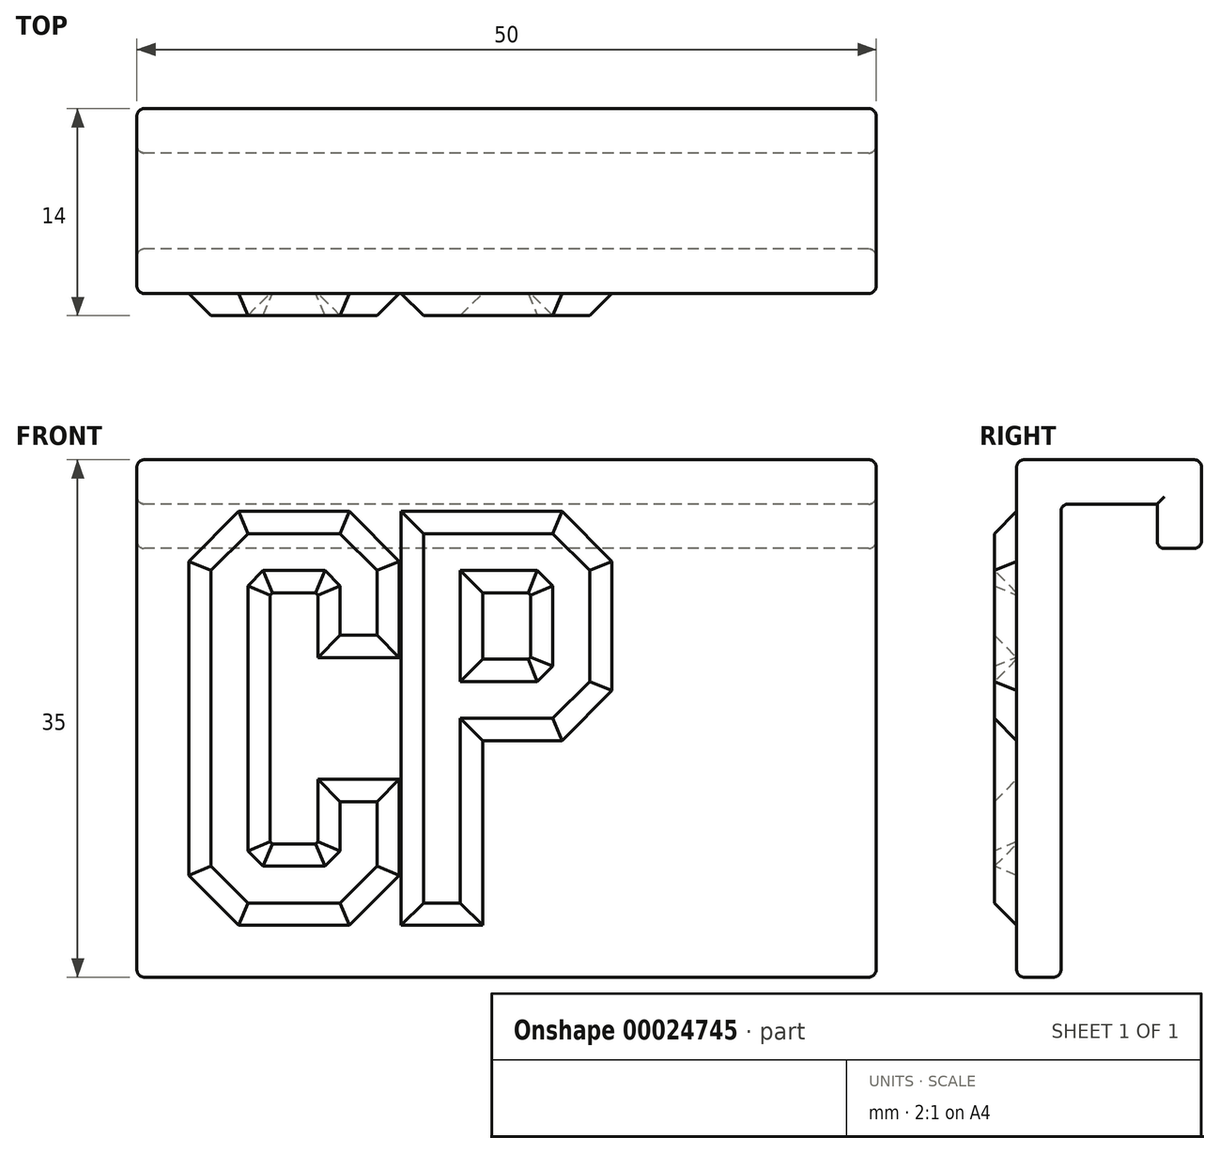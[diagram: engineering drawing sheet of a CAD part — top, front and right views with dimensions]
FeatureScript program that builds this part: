
annotation { "Feature Type Name" : "Feature", "Feature Type Description" : "" }
export const myFeature = defineFeature(function(context is Context, id is Id, definition is map)
    precondition{}
    {
        {
            var Q0;
            Q0=qCreatedBy(makeId("Right.planeOp"),FACE);
            var sketch = newSketch(context, id + "F0", { "sketchPlane" : qUnion([Q0])});
            skLineSegment(sketch, "E0", {"start": v(0, 0) * mm, "end": v(0, 35) * mm});
            skLineSegment(sketch, "E1", {"start": v(0, 35) * mm, "end": v(12.5, 35) * mm});
            skLineSegment(sketch, "E2", {"start": v(12.5, 35) * mm, "end": v(12.5, 29) * mm});
            skLineSegment(sketch, "E3", {"start": v(12.5, 29) * mm, "end": v(9.5, 29) * mm});
            skLineSegment(sketch, "E4", {"start": v(9.5, 29) * mm, "end": v(9.5, 32) * mm});
            skLineSegment(sketch, "E5", {"start": v(9.5, 32) * mm, "end": v(3, 32) * mm});
            skLineSegment(sketch, "E6", {"start": v(3, 32) * mm, "end": v(3, 0) * mm});
            skLineSegment(sketch, "E7", {"start": v(3, 0) * mm, "end": v(0, 0) * mm});
            skSolve(sketch);
        }
        {
            var Q0;
            Q0=qSketchRegion(id+"F0",true);
            extrude(context, id + "F1", {"entities" : qUnion([Q0]), "depth" : 50 * mm});
        }
        {
            var Q0;
            Q0=makeQuery(id+"F1.opExtrude","SWEPT_FACE",FACE,{"disambiguationData":[OSD([sQuery(id+"F0.wireOp",EDGE,"E0")])]});
            var sketch = newSketch(context, id + "F2", { "sketchPlane" : qUnion([Q0])});
            skLineSegment(sketch, "E8", {"start": v(17.5, 35) * mm, "end": v(17.5, 0) * mm});
            skLineSegment(sketch, "E9", {"start": v(32.5, 35) * mm, "end": v(32.5, 0) * mm});
            skLineSegment(sketch, "E10", {"start": v(0, 5) * mm, "end": v(50, 5) * mm});
            skLineSegment(sketch, "E11", {"start": v(2.5, 35) * mm, "end": v(2.5, 0) * mm});
            skLineSegment(sketch, "E12", {"start": v(47.5, 35) * mm, "end": v(47.5, 0) * mm});
            skPoint(sketch, "E13", {"position": v(2.5, 30) * mm});
            skPoint(sketch, "E14", {"position": v(32.5, 30) * mm});
            skPoint(sketch, "E15", {"position": v(47.5, 30) * mm});
            skPoint(sketch, "E16", {"position": v(47.5, 5) * mm});
            skPoint(sketch, "E17", {"position": v(32.5, 5) * mm});
            skPoint(sketch, "E18", {"position": v(2.5, 5) * mm});
            skPoint(sketch, "E19.trimOffspring.end.orphan", {"position": v(0, 30) * mm});
            skLineSegment(sketch, "E20", {"start": v(17.5, 30) * mm, "end": v(19.38, 30) * mm});
            skLineSegment(sketch, "E21", {"start": v(19.38, 5) * mm, "end": v(28.12, 5) * mm});
            skLineSegment(sketch, "E22", {"start": v(30.62, 5) * mm, "end": v(32.5, 5) * mm});
            skLineSegment(sketch, "E23", {"start": v(32.5, 5) * mm, "end": v(33.75, 5) * mm});
            skLineSegment(sketch, "E24", {"start": v(47.5, 5) * mm, "end": v(45, 5) * mm});
            skLineSegment(sketch, "E25", {"start": v(45, 5) * mm, "end": v(42.5, 5) * mm});
            skLineSegment(sketch, "E26", {"start": v(36.25, 5) * mm, "end": v(42.5, 5) * mm});
            skLineSegment(sketch, "E27", {"start": v(19.38, 30) * mm, "end": v(19.38, 5) * mm});
            skLineSegment(sketch, "E28", {"start": v(19.38, 30) * mm, "end": v(28.12, 30) * mm});
            skLineSegment(sketch, "E29", {"start": v(28.12, 30) * mm, "end": v(30.62, 27.5) * mm});
            skLineSegment(sketch, "E30", {"start": v(28.12, 5) * mm, "end": v(19.38, 5) * mm});
            skLineSegment(sketch, "E31", {"start": v(19.38, 30) * mm, "end": v(21.88, 30) * mm});
            skLineSegment(sketch, "E32", {"start": v(27.09, 27.5) * mm, "end": v(21.88, 27.5) * mm});
            skLineSegment(sketch, "E33", {"start": v(27.6, 26.98) * mm, "end": v(27.09, 27.5) * mm});
            skLineSegment(sketch, "E34", {"start": v(27.6, 26.98) * mm, "end": v(28.13, 26.46) * mm});
            skPoint(sketch, "E35.orphan", {"position": v(29.38, 28.75) * mm});
            skPoint(sketch, "E36.orphan", {"position": v(28.12, 27.5) * mm});
            skPoint(sketch, "E37.orphan", {"position": v(28.12, 18.75) * mm});
            skPoint(sketch, "E38.orphan", {"position": v(30.62, 30) * mm});
            skLineSegment(sketch, "E39", {"start": v(17.5, 5) * mm, "end": v(16.25, 5) * mm});
            skLineSegment(sketch, "E40", {"start": v(33.75, 5) * mm, "end": v(33.75, 30) * mm});
            skLineSegment(sketch, "E41", {"start": v(5, 5) * mm, "end": v(2.5, 5) * mm});
            skLineSegment(sketch, "E42", {"start": v(33.75, 30) * mm, "end": v(45, 30) * mm});
            skLineSegment(sketch, "E43", {"start": v(45, 30) * mm, "end": v(45, 5) * mm});
            skLineSegment(sketch, "E44", {"start": v(37.29, 18.75) * mm, "end": v(42.5, 18.75) * mm});
            skLineSegment(sketch, "E45", {"start": v(36.25, 16.25) * mm, "end": v(41.46, 16.25) * mm});
            skLineSegment(sketch, "E46", {"start": v(45, 16.25) * mm, "end": v(45, 7.5) * mm});
            skLineSegment(sketch, "E47", {"start": v(45, 23.12) * mm, "end": v(45, 27.5) * mm});
            skPoint(sketch, "E48.orphan", {"position": v(35, 28.75) * mm});
            skPoint(sketch, "E49.orphan", {"position": v(36.25, 27.5) * mm});
            skPoint(sketch, "E50.orphan", {"position": v(42.5, 27.5) * mm});
            skPoint(sketch, "E51.orphan", {"position": v(36.25, 18.75) * mm});
            skPoint(sketch, "E52.orphan", {"position": v(36.25, 7.5) * mm});
            skPoint(sketch, "E53.orphan", {"position": v(42.5, 16.25) * mm});
            skPoint(sketch, "E54.start.orphan", {"position": v(42.5, 7.5) * mm});
            skLineSegment(sketch, "E55", {"start": v(5, 7.5) * mm, "end": v(5, 27.5) * mm});
            skLineSegment(sketch, "E56", {"start": v(7.5, 30) * mm, "end": v(13.75, 30) * mm});
            skLineSegment(sketch, "E57", {"start": v(7.5, 26.46) * mm, "end": v(7.5, 8.54) * mm});
            skLineSegment(sketch, "E58", {"start": v(7.5, 30) * mm, "end": v(5, 27.5) * mm});
            skLineSegment(sketch, "E59", {"start": v(5, 7.5) * mm, "end": v(7.5, 5) * mm});
            skLineSegment(sketch, "E60", {"start": v(16.25, 7.5) * mm, "end": v(13.75, 5) * mm});
            skLineSegment(sketch, "E61", {"start": v(16.25, 27.5) * mm, "end": v(13.75, 30) * mm});
            skLineSegment(sketch, "E62", {"start": v(8.54, 27.5) * mm, "end": v(12.71, 27.5) * mm});
            skLineSegment(sketch, "E63", {"start": v(8.54, 7.5) * mm, "end": v(12.71, 7.5) * mm});
            skLineSegment(sketch, "E64", {"start": v(7.5, 26.46) * mm, "end": v(8.54, 27.5) * mm});
            skPoint(sketch, "E65.orphan", {"position": v(7.5, 27.5) * mm});
            skLineSegment(sketch, "E66", {"start": v(7.5, 8.54) * mm, "end": v(8.54, 7.5) * mm});
            skPoint(sketch, "E67.orphan", {"position": v(7.5, 7.5) * mm});
            skPoint(sketch, "E68.start.orphan", {"position": v(16.25, 30) * mm});
            skPoint(sketch, "E69.orphan", {"position": v(5, 30) * mm});
            skLineSegment(sketch, "E70", {"start": v(16.25, 23.12) * mm, "end": v(16.25, 27.5) * mm});
            skLineSegment(sketch, "E71", {"start": v(16.25, 7.5) * mm, "end": v(16.25, 11.87) * mm});
            skLineSegment(sketch, "E72", {"start": v(16.25, 11.87) * mm, "end": v(13.75, 11.87) * mm});
            skLineSegment(sketch, "E73", {"start": v(13.75, 11.87) * mm, "end": v(13.75, 8.54) * mm});
            skLineSegment(sketch, "E74", {"start": v(13.75, 26.46) * mm, "end": v(13.75, 23.12) * mm});
            skLineSegment(sketch, "E75", {"start": v(13.75, 23.12) * mm, "end": v(16.25, 23.12) * mm});
            skLineSegment(sketch, "E76", {"start": v(13.75, 26.46) * mm, "end": v(12.71, 27.5) * mm});
            skPoint(sketch, "E77.orphan", {"position": v(13.75, 27.5) * mm});
            skLineSegment(sketch, "E78", {"start": v(12.71, 7.5) * mm, "end": v(13.75, 8.54) * mm});
            skPoint(sketch, "E79.orphan", {"position": v(13.75, 7.5) * mm});
            skLineSegment(sketch, "E80", {"start": v(21.88, 20) * mm, "end": v(21.88, 27.5) * mm});
            skLineSegment(sketch, "E81", {"start": v(21.88, 17.5) * mm, "end": v(21.88, 5) * mm});
            skLineSegment(sketch, "E82", {"start": v(21.88, 20) * mm, "end": v(27.09, 20) * mm});
            skLineSegment(sketch, "E83", {"start": v(21.88, 17.5) * mm, "end": v(28.12, 17.5) * mm});
            skLineSegment(sketch, "E84", {"start": v(28.12, 17.5) * mm, "end": v(30.62, 20) * mm});
            skLineSegment(sketch, "E85", {"start": v(30.62, 20) * mm, "end": v(30.62, 27.5) * mm});
            skLineSegment(sketch, "E86", {"start": v(28.13, 26.46) * mm, "end": v(28.13, 21.04) * mm});
            skLineSegment(sketch, "E87", {"start": v(27.09, 20) * mm, "end": v(28.13, 21.04) * mm});
            skLineSegment(sketch, "E88", {"start": v(37.29, 18.75) * mm, "end": v(36.25, 18.75) * mm});
            skLineSegment(sketch, "E89", {"start": v(33.75, 27.5) * mm, "end": v(33.75, 7.5) * mm});
            skLineSegment(sketch, "E90", {"start": v(36.25, 16.25) * mm, "end": v(36.25, 7.5) * mm});
            skLineSegment(sketch, "E91", {"start": v(36.25, 7.5) * mm, "end": v(45, 7.5) * mm});
            skLineSegment(sketch, "E92", {"start": v(36.25, 27.5) * mm, "end": v(36.25, 18.75) * mm});
            skLineSegment(sketch, "E93", {"start": v(36.25, 27.5) * mm, "end": v(45, 27.5) * mm});
            skLineSegment(sketch, "E94", {"start": v(41.46, 16.25) * mm, "end": v(42.5, 16.25) * mm});
            skLineSegment(sketch, "E95", {"start": v(42.5, 18.75) * mm, "end": v(45, 18.75) * mm});
            skLineSegment(sketch, "E96", {"start": v(45, 18.75) * mm, "end": v(45, 16.25) * mm});
            skLineSegment(sketch, "E97", {"start": v(42.5, 16.25) * mm, "end": v(45, 16.25) * mm});
            skSolve(sketch);
        }
        {
            var Q0;
            Q0=makeQuery(id+"F2.imprint","IMPRINT",FACE,{"disambiguationData":[TD([[makeQuery(id+"F2.imprint","IMPRINT",EDGE,{"derivedFrom":sQuery(id+"F2.wireOp",EDGE,"E55")}),-1.0]])]});
            var Q1;
            {var subQ6=sQuery(id+"F2.wireOp",EDGE,"E27");Q1=makeQuery(id+"F2.imprint","IMPRINT",FACE,{"disambiguationData":[TD([[makeQuery(id+"F2.imprint","IMPRINT",EDGE,{"derivedFrom":subQ6}),1.0]])]});}
            var Q2;
            {var subQ2=sQuery(id+"F2.wireOp",EDGE,"E25");Q2=makeQuery(id+"F2.imprint","IMPRINT",FACE,{"disambiguationData":[TD([[makeQuery(id+"F2.imprint","IMPRINT",EDGE,{"derivedFrom":subQ2}),-1.0]])]});}
            extrude(context, id + "F3", {"entities" : qUnion([Q0, Q1, Q2]), "operationType" : NewBodyOperationType.ADD, "depth" : 1.5 * mm});
        }
        {
            var Q0;
            Q0=makeQuery(id+"F1.opExtrude","CAP_FACE",FACE,{"disambiguationData":[OSD([sQuery(id+"F0.wireOp",EDGE,"E0"),sQuery(id+"F0.wireOp",EDGE,"E1"),sQuery(id+"F0.wireOp",EDGE,"E2"),sQuery(id+"F0.wireOp",EDGE,"E3"),sQuery(id+"F0.wireOp",EDGE,"E4"),sQuery(id+"F0.wireOp",EDGE,"E5"),sQuery(id+"F0.wireOp",EDGE,"E6"),sQuery(id+"F0.wireOp",EDGE,"E7")])],"isStart":false});
            var Q1;
            Q1=makeQuery(id+"F1.opExtrude","SWEPT_FACE",FACE,{"disambiguationData":[OSD([sQuery(id+"F0.wireOp",EDGE,"E1")])]});
            var Q2;
            Q2=makeQuery(id+"F1.opExtrude","SWEPT_FACE",FACE,{"disambiguationData":[OSD([sQuery(id+"F0.wireOp",EDGE,"E7")])]});
            var Q3;
            Q3=makeQuery(id+"F1.opExtrude","CAP_FACE",FACE,{"disambiguationData":[OSD([sQuery(id+"F0.wireOp",EDGE,"E0"),sQuery(id+"F0.wireOp",EDGE,"E1"),sQuery(id+"F0.wireOp",EDGE,"E2"),sQuery(id+"F0.wireOp",EDGE,"E3"),sQuery(id+"F0.wireOp",EDGE,"E4"),sQuery(id+"F0.wireOp",EDGE,"E5"),sQuery(id+"F0.wireOp",EDGE,"E6"),sQuery(id+"F0.wireOp",EDGE,"E7")])],"isStart":true});
            var Q4;
            Q4=makeQuery(id+"F1.opExtrude","SWEPT_FACE",FACE,{"disambiguationData":[OSD([sQuery(id+"F0.wireOp",EDGE,"E6")])]});
            var Q5;
            Q5=makeQuery(id+"F1.opExtrude","SWEPT_FACE",FACE,{"disambiguationData":[OSD([sQuery(id+"F0.wireOp",EDGE,"E3")])]});
            var Q6;
            Q6=makeQuery(id+"F1.opExtrude","SWEPT_FACE",FACE,{"disambiguationData":[OSD([sQuery(id+"F0.wireOp",EDGE,"E2")])]});
            fillet(context, id + "F4", {"entities" : qUnion([Q0, Q1, Q2, Q3, Q4, Q5, Q6]), "radius" : .5 * mm, "tangentPropagation" : true, "allowEdgeOverflow" : false});
        }
        {
            var Q0;
            {var subQ0=sQuery(id+"F0.wireOp",EDGE,"E0");var subQ5=sQuery(id+"F0.wireOp",EDGE,"E1");Q0=makeQuery(id+"F3.boolean.opBoolean","SPLIT",FACE,{"disambiguationData":[TD([makeQuery(id+"F1.opExtrude","SWEPT_FACE",FACE,{"disambiguationData":[OSD([subQ5])]})])],"derivedFrom":makeQuery(id+"F1.opExtrude","SWEPT_FACE",FACE,{"disambiguationData":[OSD([subQ0])]})});}
            var Q1;
            Q1=makeQuery(id+"F3.boolean.opBoolean","SPLIT",FACE,{"disambiguationData":[TD([makeQuery(id+"F3.opExtrude","SWEPT_FACE",FACE,{"disambiguationData":[OSD([sQuery(id+"F2.wireOp",EDGE,"E32")])]})])],"derivedFrom":makeQuery(id+"F1.opExtrude","SWEPT_FACE",FACE,{"disambiguationData":[OSD([sQuery(id+"F0.wireOp",EDGE,"E0")])]})});
            chamfer(context, id + "F5", {"entities" : qUnion([Q0, Q1]), "width" : 1.5 * mm, "tangentPropagation" : true});
        }
    });
